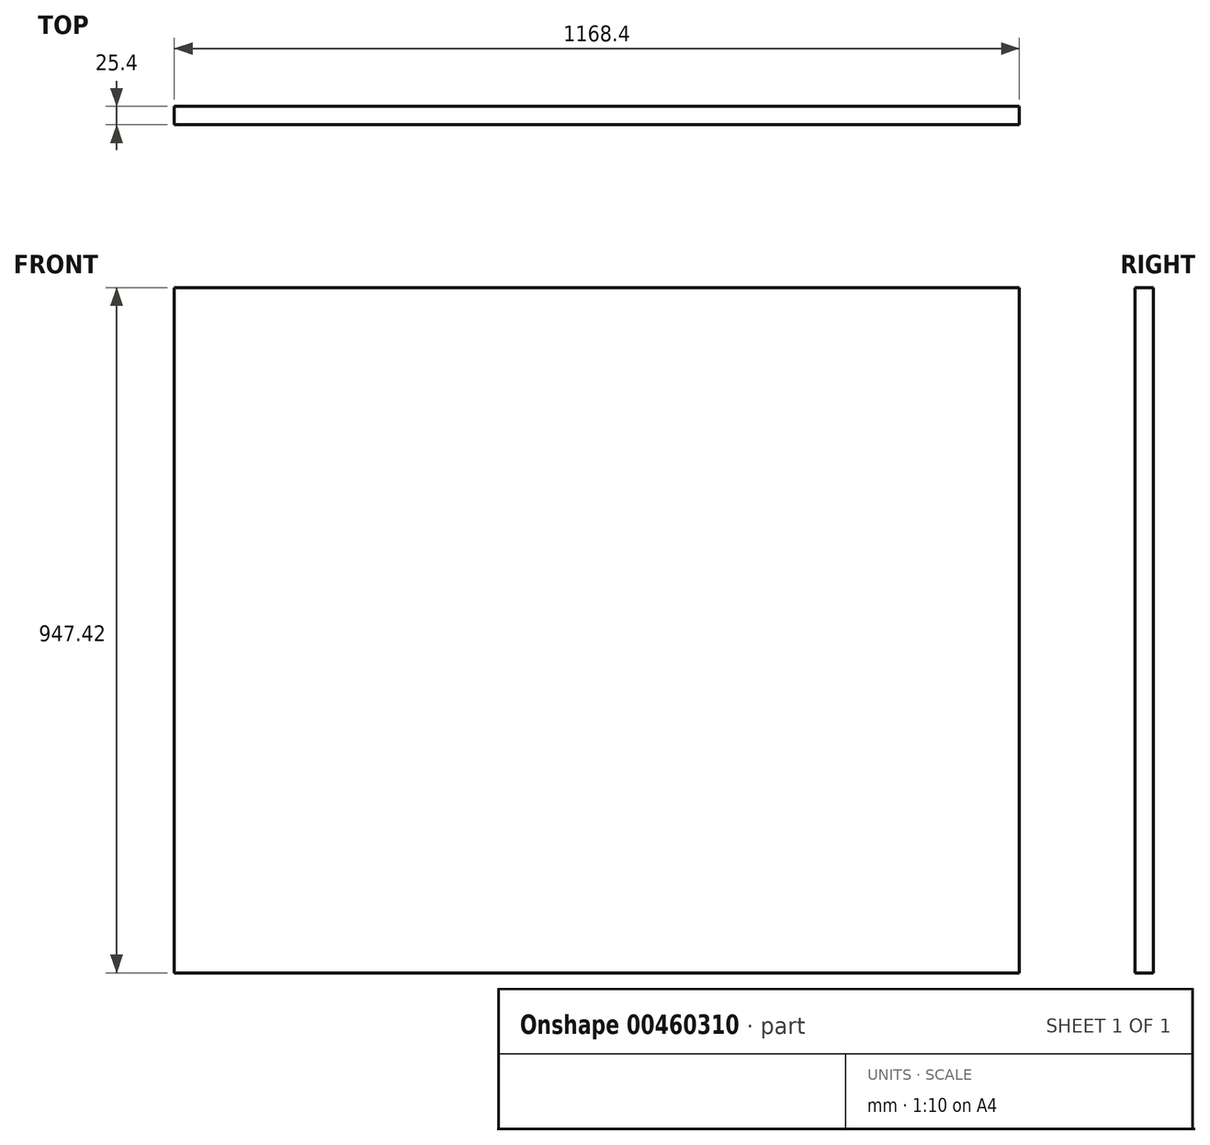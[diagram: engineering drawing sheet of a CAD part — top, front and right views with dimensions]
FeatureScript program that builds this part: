
annotation { "Feature Type Name" : "Feature", "Feature Type Description" : "" }
export const myFeature = defineFeature(function(context is Context, id is Id, definition is map)
    precondition{}
    {
        {
            var Q0;
            Q0=qCreatedBy(makeId("Front.planeOp"),FACE);
            var sketch = newSketch(context, id + "F0", { "sketchPlane" : qUnion([Q0])});
            skLineSegment(sketch, "E0.bottom", {"start": v(-584.2, 473.71) * mm, "end": v(584.2, 473.71) * mm});
            skLineSegment(sketch, "E0.top", {"start": v(-584.2, -473.71) * mm, "end": v(584.2, -473.71) * mm});
            skLineSegment(sketch, "E0.left", {"start": v(-584.2, 473.71) * mm, "end": v(-584.2, -473.71) * mm});
            skLineSegment(sketch, "E0.right", {"start": v(584.2, 473.71) * mm, "end": v(584.2, -473.71) * mm});
            skSolve(sketch);
        }
        {
            var Q0;
            Q0 = qSketchRegion(id + "F0", true);
            extrude(context, id + "F1", {"entities" : qUnion([Q0]), "depth" : 25.4 * mm});
        }
    });
